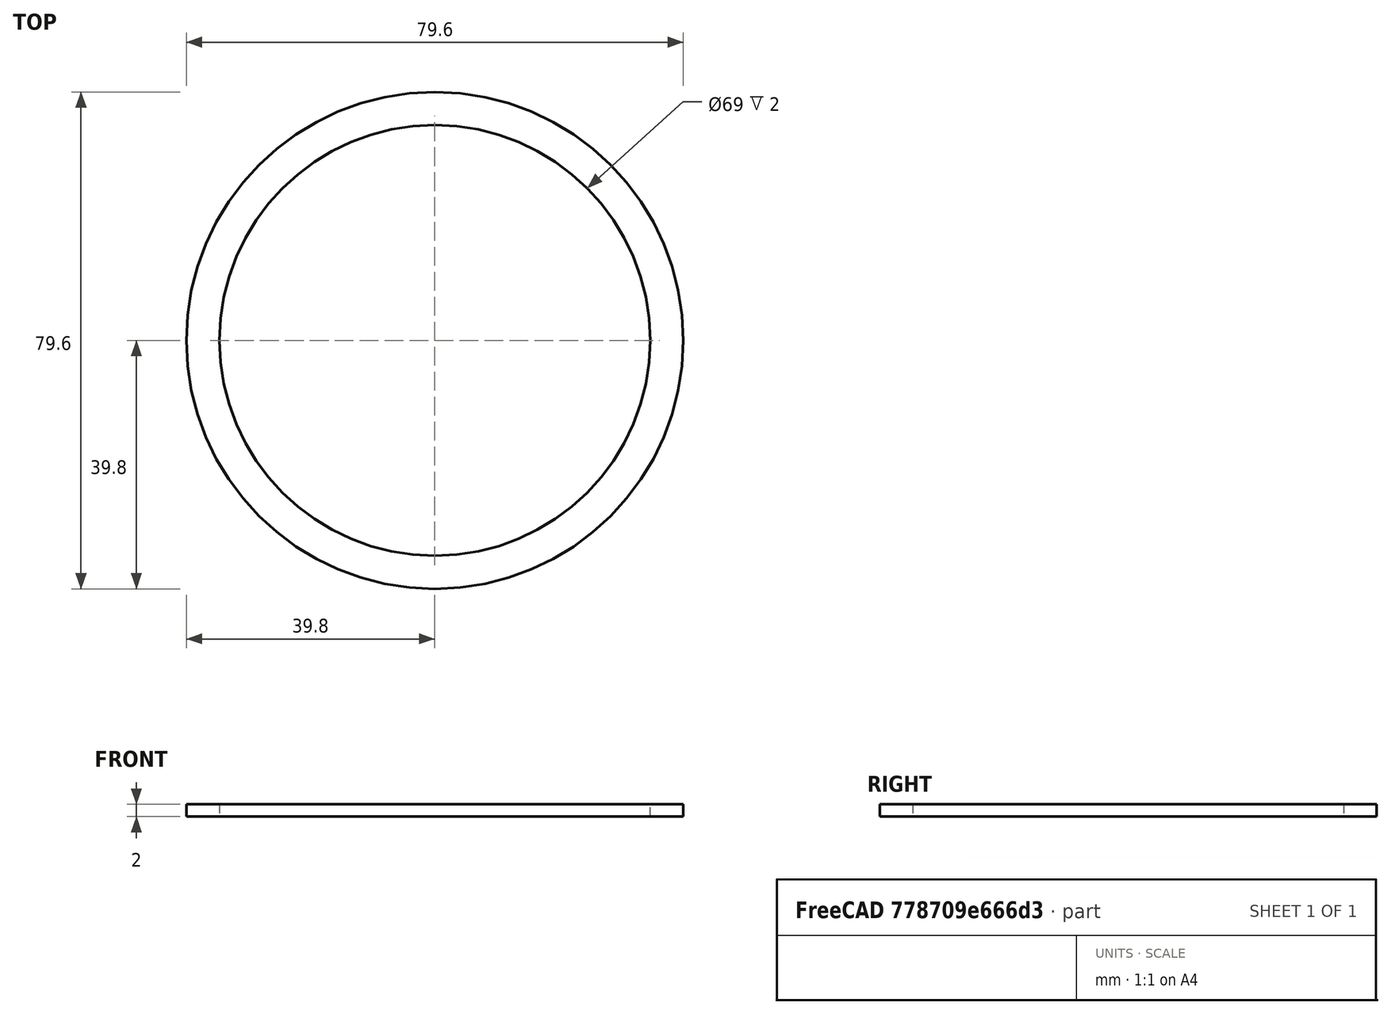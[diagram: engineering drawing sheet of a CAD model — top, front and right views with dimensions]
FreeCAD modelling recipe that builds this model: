
FCSTD DOCUMENT  (FreeCAD 0.19R24276 (Git))
Label: Ring_69__79_5_h2
License: All rights reserved
LicenseURL: http://en.wikipedia.org/wiki/All_rights_reserved
objects: Sketcher::SketchObject×1, PartDesign::Pad×1, PartDesign::Body×1
note: 4 computed .brp shape members not serialized (recipe doc carries the construction recipe); baked Part::Feature solids carry a one-line shape summary decoded from their .brp

FEATURE [Sketcher::SketchObject] Sketch
  FullyConstrained = true
  MapMode = 5
  Support = -> [XY_Plane]
  sketch-geometry (2):
    g0: Circle CenterX=0 CenterY=0 CenterZ=0 NormalX=0 NormalY=0 NormalZ=1 AngleXU=0 Radius=39.8
    g1: Circle CenterX=0 CenterY=0 CenterZ=0 NormalX=0 NormalY=0 NormalZ=1 AngleXU=0 Radius=34.5
  constraints (4):
    c: Coincident(g0,g-1)
    c: Coincident(g1,g0)
    c: Diameter(g0) = 79.6
    c: Diameter(g1) = 69
FEATURE [PartDesign::Pad] Pad
  Direction = (1,1,1)
  Length = 2
  Length2 = 100
  Profile = -> Sketch
  Type = 0
FEATURE [PartDesign::Body] Body
  Group = -> [Sketch,Pad]
  Origin = -> Origin
  Tip = -> Pad
